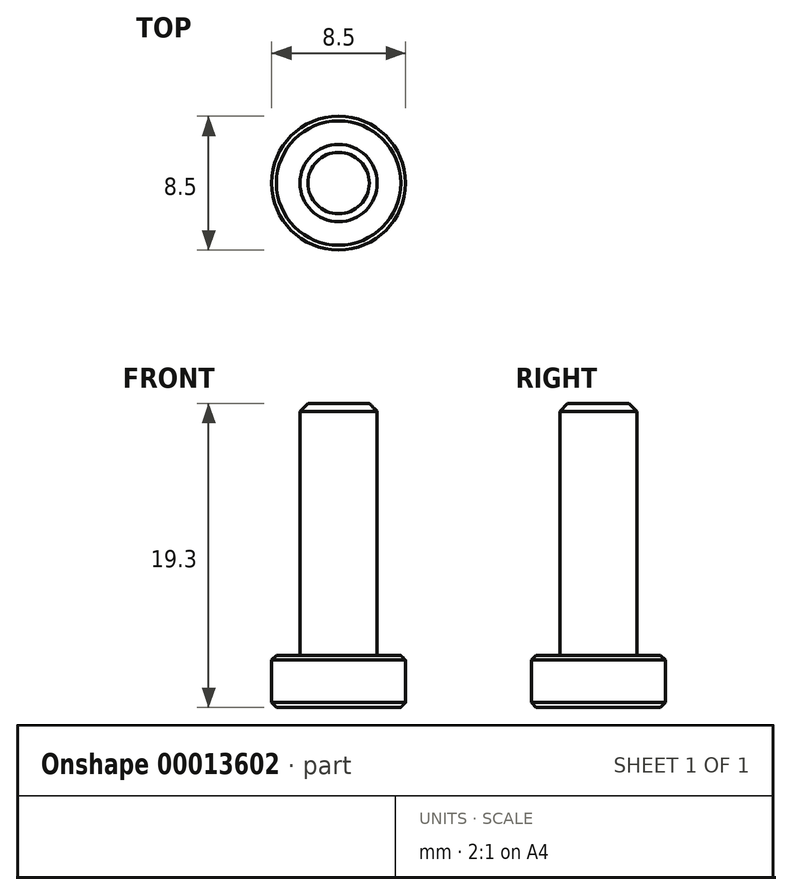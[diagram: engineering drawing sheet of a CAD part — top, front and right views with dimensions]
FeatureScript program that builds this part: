
annotation { "Feature Type Name" : "Feature", "Feature Type Description" : "" }
export const myFeature = defineFeature(function(context is Context, id is Id, definition is map)
    precondition{}
    {
        {
            var Q0;
            Q0=qCreatedBy(makeId("Top.planeOp"),FACE);
            var sketch = newSketch(context, id + "F0", { "sketchPlane" : qUnion([Q0])});
            skCircle(sketch, "E0", {"center": v(0, 0) * mm, "radius": 4.25 * mm});
            skCircle(sketch, "E1", {"center": v(0, 0) * mm, "radius": 2.45 * mm});
            skSolve(sketch);
        }
        {
            var Q0;
            Q0=makeQuery(id+"F0.imprint","IMPRINT",FACE,{"disambiguationData":[TD([[makeQuery(id+"F0.imprint","IMPRINT",EDGE,{"derivedFrom":sQuery(id+"F0.wireOp",EDGE,"E0")}),1.0]])]});
            var Q1;
            Q1=makeQuery(id+"F0.imprint","IMPRINT",FACE,{"disambiguationData":[TD([[makeQuery(id+"F0.imprint","IMPRINT",EDGE,{"derivedFrom":sQuery(id+"F0.wireOp",EDGE,"E1")}),1.0]])]});
            extrude(context, id + "F1", {"entities" : qUnion([Q0, Q1]), "oppositeDirection" : true, "depth" : 3.3 * mm});
        }
        {
            var Q0;
            Q0=makeQuery(id+"F0.imprint","IMPRINT",FACE,{"disambiguationData":[TD([[makeQuery(id+"F0.imprint","IMPRINT",EDGE,{"derivedFrom":sQuery(id+"F0.wireOp",EDGE,"E1")}),1.0]])]});
            extrude(context, id + "F2", {"entities" : qUnion([Q0]), "operationType" : NewBodyOperationType.ADD, "depth" : 16 * mm});
        }
        {
            var Q0;
            Q0=makeQuery(id+"F2.opExtrude","CAP_EDGE",EDGE,{"disambiguationData":[OSD([sQuery(id+"F0.wireOp",EDGE,"E1")])],"isStart":true});
            var Q1;
            Q1=makeQuery(id+"F2.opExtrude","CAP_EDGE",EDGE,{"disambiguationData":[OSD([sQuery(id+"F0.wireOp",EDGE,"E1")])],"isStart":false});
            chamfer(context, id + "F3", {"entities" : qUnion([Q0, Q1]), "width" : 0.5 * mm, "tangentPropagation" : true});
        }
        {
            var Q0;
            Q0=makeQuery(id+"F1.opExtrude","CAP_EDGE",EDGE,{"disambiguationData":[OSD([sQuery(id+"F0.wireOp",EDGE,"E0")])],"isStart":true});
            var Q1;
            Q1=makeQuery(id+"F1.opExtrude","CAP_EDGE",EDGE,{"disambiguationData":[OSD([sQuery(id+"F0.wireOp",EDGE,"E0")])],"isStart":false});
            chamfer(context, id + "F4", {"entities" : qUnion([Q0, Q1]), "width" : 0.3 * mm, "tangentPropagation" : true});
        }
    });
